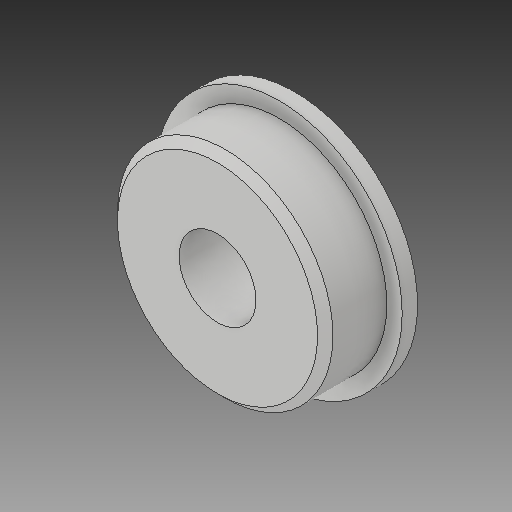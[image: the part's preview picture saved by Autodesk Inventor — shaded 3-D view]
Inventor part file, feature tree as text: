
AUTODESK INVENTOR PART (.ipt)
format: ipt  version: 2018 (Build 220112000, 112)  size: 124,928 bytes
history: native  units: mm
features: other x3, sketch x2
ambient origin geometry x8: Origin, YZ Plane, XZ Plane, XY Plane, X Axis, Y Axis, Z Axis, Center Point
bodies: Solid1 (feature_tree)
feature tree (5):
  other  "Flanged Bearing.ipt"
  other  "Solid1::Flanged Bearing.ipt"
  other  "TaggingFeature1"
  sketch  "Sketch1"  dims[d0=10.0mm]
  sketch  "Sketch2"
